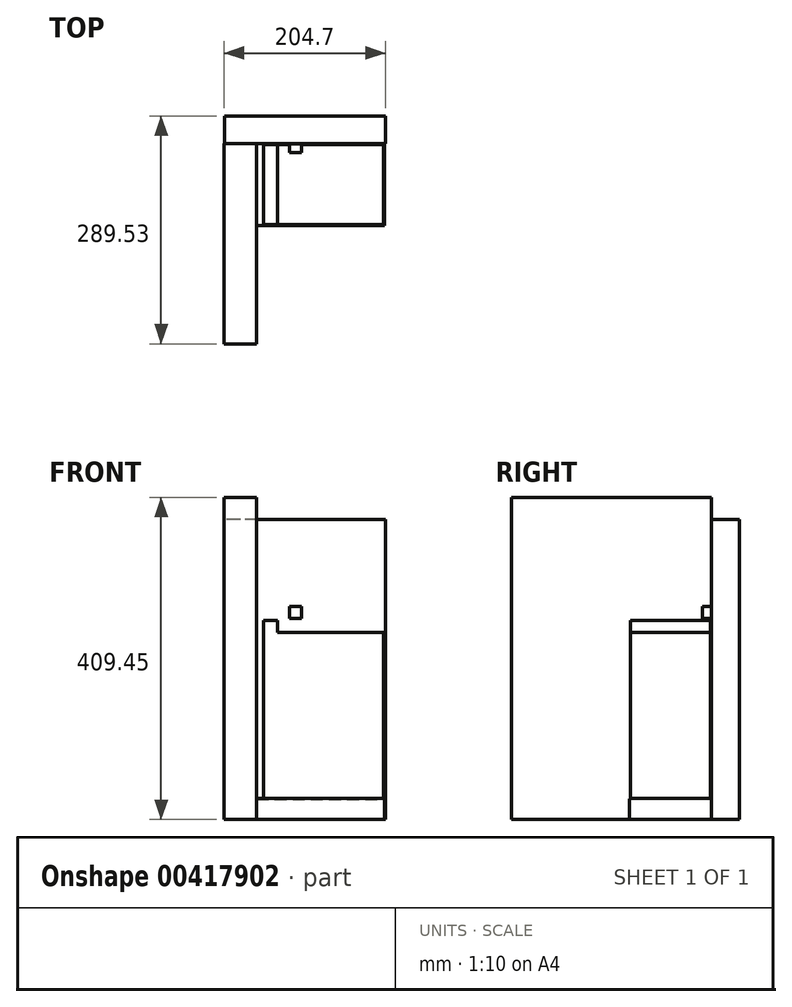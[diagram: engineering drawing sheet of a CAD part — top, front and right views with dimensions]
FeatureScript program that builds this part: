
annotation { "Feature Type Name" : "Feature", "Feature Type Description" : "" }
export const myFeature = defineFeature(function(context is Context, id is Id, definition is map)
    precondition{}
    {
        {
            var Q0;
            Q0=qCreatedBy(makeId("Top.planeOp"),FACE);
            var sketch = newSketch(context, id + "F0", { "sketchPlane" : qUnion([Q0])});
            skLineSegment(sketch, "E0.bottom", {"start": v(0, 0) * mm, "end": v(162.56, 0) * mm});
            skLineSegment(sketch, "E0.top", {"start": v(0, -104.14) * mm, "end": v(162.56, -104.14) * mm});
            skLineSegment(sketch, "E0.left", {"start": v(0, 0) * mm, "end": v(0, -104.14) * mm});
            skLineSegment(sketch, "E0.right", {"start": v(162.56, 0) * mm, "end": v(162.56, -104.14) * mm});
            skSolve(sketch);
        }
        {
            var Q0;
            Q0 = qSketchRegion(id + "F0", true);
            extrude(context, id + "F1", {"entities" : qUnion([Q0]), "depth" : 26.67 * mm});
        }
        {
            var Q0;
            Q0=makeQuery(id+"F1.opExtrude","CAP_FACE",FACE,{"disambiguationData":[OSD([sQuery(id+"F0.wireOp",EDGE,"E0.bottom"),sQuery(id+"F0.wireOp",EDGE,"E0.top"),sQuery(id+"F0.wireOp",EDGE,"E0.left"),sQuery(id+"F0.wireOp",EDGE,"E0.right")])],"isStart":false});
            fillet(context, id + "F2", {"entities" : qUnion([Q0]), "radius" : 1.27 * mm, "tangentPropagation" : true, "allowEdgeOverflow" : false});
        }
        {
            var Q0;
            Q0=qCreatedBy(makeId("Top.planeOp"),FACE);
            var sketch = newSketch(context, id + "F3", { "sketchPlane" : qUnion([Q0])});
            skLineSegment(sketch, "E1.bottom", {"start": v(0, 0) * mm, "end": v(-41.22, 0) * mm});
            skLineSegment(sketch, "E1.top", {"start": v(0, -254.2) * mm, "end": v(-41.22, -254.2) * mm});
            skLineSegment(sketch, "E1.left", {"start": v(0, 0) * mm, "end": v(0, -254.2) * mm});
            skLineSegment(sketch, "E1.right", {"start": v(-41.22, 0) * mm, "end": v(-41.22, -254.2) * mm});
            skSolve(sketch);
        }
        {
            var Q0;
            Q0 = qSketchRegion(id + "F3", true);
            extrude(context, id + "F4", {"entities" : qUnion([Q0]), "operationType" : NewBodyOperationType.ADD, "depth" : 409.45 * mm});
        }
        {
            var Q0;
            Q0=qCreatedBy(makeId("Top.planeOp"),FACE);
            var sketch = newSketch(context, id + "F5", { "sketchPlane" : qUnion([Q0])});
            skLineSegment(sketch, "E2.bottom", {"start": v(163.48, 0) * mm, "end": v(-40.7, 0) * mm});
            skLineSegment(sketch, "E2.top", {"start": v(163.48, 35.32) * mm, "end": v(-40.7, 35.32) * mm});
            skLineSegment(sketch, "E2.left", {"start": v(163.48, 0) * mm, "end": v(163.48, 35.32) * mm});
            skLineSegment(sketch, "E2.right", {"start": v(-40.7, 0) * mm, "end": v(-40.7, 35.32) * mm});
            skSolve(sketch);
        }
        {
            var Q0;
            Q0 = qSketchRegion(id + "F5", true);
            extrude(context, id + "F6", {"entities" : qUnion([Q0]), "operationType" : NewBodyOperationType.ADD, "depth" : 381 * mm});
        }
        {
            var Q0;
            Q0=makeQuery(id+"F6.opExtrude","SWEPT_FACE",FACE,{"disambiguationData":[OSD([sQuery(id+"F5.wireOp",EDGE,"E2.bottom")])]});
            var sketch = newSketch(context, id + "F7", { "sketchPlane" : qUnion([Q0])});
            skLineSegment(sketch, "E3.bottom", {"start": v(41.91, 255.27) * mm, "end": v(57.15, 255.27) * mm});
            skLineSegment(sketch, "E3.top", {"start": v(41.9, 270.5) * mm, "end": v(57.15, 270.5) * mm});
            skLineSegment(sketch, "E3.left", {"start": v(41.91, 255.27) * mm, "end": v(41.9, 270.5) * mm});
            skLineSegment(sketch, "E3.right", {"start": v(57.15, 255.27) * mm, "end": v(57.15, 270.5) * mm});
            skSolve(sketch);
        }
        {
            var Q0;
            Q0 = qSketchRegion(id + "F7", true);
            extrude(context, id + "F8", {"entities" : qUnion([Q0]), "operationType" : NewBodyOperationType.ADD, "depth" : 11.43 * mm});
        }
        {
            var Q0;
            Q0=makeQuery(id+"F1.opExtrude","CAP_FACE",FACE,{"disambiguationData":[OSD([sQuery(id+"F0.wireOp",EDGE,"E0.bottom"),sQuery(id+"F0.wireOp",EDGE,"E0.top"),sQuery(id+"F0.wireOp",EDGE,"E0.left"),sQuery(id+"F0.wireOp",EDGE,"E0.right")])],"isStart":false});
            var sketch = newSketch(context, id + "F9", { "sketchPlane" : qUnion([Q0])});
            skLineSegment(sketch, "E4.bottom", {"start": v(161.3, -102.87) * mm, "end": v(8.9, -102.87) * mm});
            skLineSegment(sketch, "E4.top", {"start": v(161.3, -1.27) * mm, "end": v(8.9, -1.27) * mm});
            skLineSegment(sketch, "E4.left", {"start": v(161.3, -102.87) * mm, "end": v(161.3, -1.27) * mm});
            skLineSegment(sketch, "E4.right", {"start": v(8.9, -102.87) * mm, "end": v(8.9, -1.27) * mm});
            skSolve(sketch);
        }
        {
            var Q0;
            Q0 = qSketchRegion(id + "F9", true);
            extrude(context, id + "F10", {"entities" : qUnion([Q0]), "depth" : 226.06 * mm});
        }
        {
            var Q0;
            Q0=makeQuery(id+"F10.opExtrude","CAP_FACE",FACE,{"disambiguationData":[OSD([sQuery(id+"F9.wireOp",EDGE,"E4.bottom"),sQuery(id+"F9.wireOp",EDGE,"E4.top"),sQuery(id+"F9.wireOp",EDGE,"E4.left"),sQuery(id+"F9.wireOp",EDGE,"E4.right")])],"isStart":false});
            var sketch = newSketch(context, id + "F11", { "sketchPlane" : qUnion([Q0])});
            skLineSegment(sketch, "E5.bottom", {"start": v(161.3, -102.87) * mm, "end": v(26.67, -102.87) * mm});
            skLineSegment(sketch, "E5.top", {"start": v(161.3, -1.27) * mm, "end": v(26.67, -1.27) * mm});
            skLineSegment(sketch, "E5.left", {"start": v(161.3, -102.87) * mm, "end": v(161.3, -1.27) * mm});
            skLineSegment(sketch, "E5.right", {"start": v(26.67, -102.87) * mm, "end": v(26.67, -1.27) * mm});
            skSolve(sketch);
        }
        {
            var Q0;
            Q0 = qSketchRegion(id + "F11", true);
            extrude(context, id + "F12", {"entities" : qUnion([Q0]), "operationType" : NewBodyOperationType.REMOVE, "oppositeDirection" : true, "depth" : 15.24 * mm});
        }
    });
